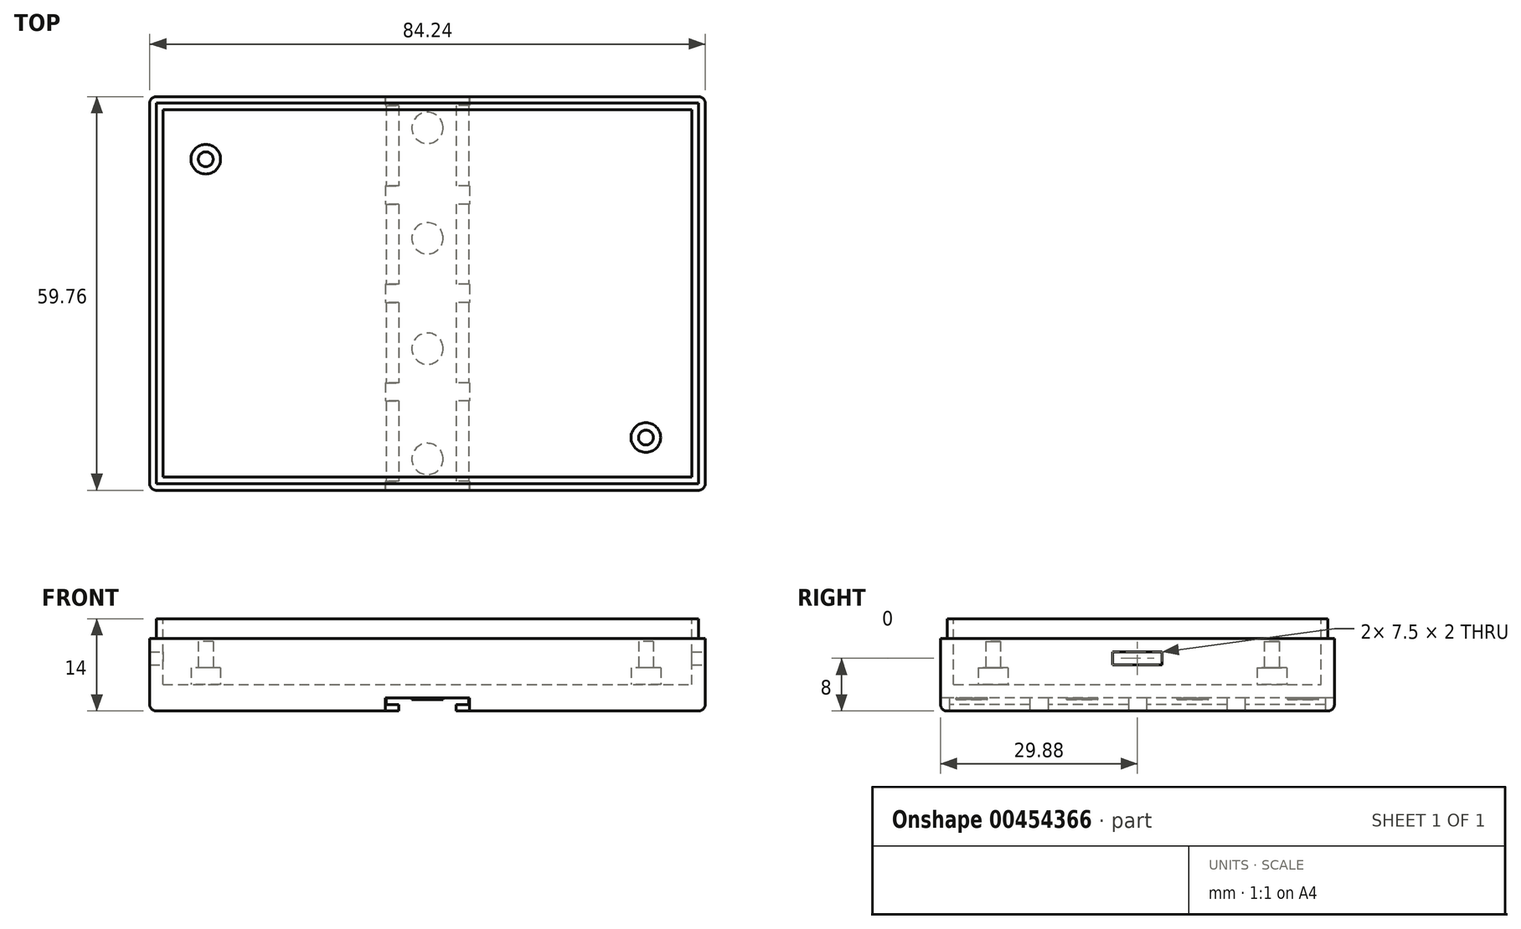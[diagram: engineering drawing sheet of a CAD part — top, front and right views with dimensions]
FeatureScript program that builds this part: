
annotation { "Feature Type Name" : "Feature", "Feature Type Description" : "" }
export const myFeature = defineFeature(function(context is Context, id is Id, definition is map)
    precondition{}
    {
        {
            var Q0;
            Q0=qCreatedBy(makeId("Top.planeOp"),FACE);
            var sketch = newSketch(context, id + "F0", { "sketchPlane" : qUnion([Q0])});
            skLineSegment(sketch, "E0.bottom", {"start": v(38.12, 25.88) * mm, "end": v(-38.12, 25.88) * mm});
            skLineSegment(sketch, "E0.top", {"start": v(38.12, -25.88) * mm, "end": v(-38.12, -25.88) * mm});
            skLineSegment(sketch, "E0.left", {"start": v(38.12, 25.88) * mm, "end": v(38.12, -25.88) * mm});
            skLineSegment(sketch, "E0.right", {"start": v(-38.12, 25.88) * mm, "end": v(-38.12, -25.88) * mm});
            skPoint(sketch, "E0.middle", {"position": v(0, 0) * mm});
            skLineSegment(sketch, "E1.bottom", {"start": v(42.13, 29.88) * mm, "end": v(-42.12, 29.87) * mm});
            skLineSegment(sketch, "E1.top", {"start": v(42.13, -29.87) * mm, "end": v(-42.12, -29.88) * mm});
            skLineSegment(sketch, "E1.left", {"start": v(42.13, 29.88) * mm, "end": v(42.13, -29.87) * mm});
            skLineSegment(sketch, "E1.right", {"start": v(-42.12, 29.87) * mm, "end": v(-42.12, -29.88) * mm});
            skSolve(sketch);
        }
        {
            var Q0;
            Q0=makeQuery(id+"F0.imprint","IMPRINT",FACE,{"disambiguationData":[TD([[makeQuery(id+"F0.imprint","IMPRINT",EDGE,{"derivedFrom":sQuery(id+"F0.wireOp",EDGE,"E0.bottom")}),1.0]])]});
            var Q1;
            Q1=makeQuery(id+"F0.imprint","IMPRINT",FACE,{"disambiguationData":[TD([[makeQuery(id+"F0.imprint","IMPRINT",EDGE,{"derivedFrom":sQuery(id+"F0.wireOp",EDGE,"E0.bottom")}),-1.0]])]});
            extrude(context, id + "F1", {"entities" : qUnion([Q0, Q1]), "depth" : 14 * mm});
        }
        {
            var Q0;
            Q0=makeQuery(id+"F1.opExtrude","CAP_FACE",FACE,{"disambiguationData":[OSD([sQuery(id+"F0.wireOp",EDGE,"E1.bottom"),sQuery(id+"F0.wireOp",EDGE,"E1.top"),sQuery(id+"F0.wireOp",EDGE,"E1.left"),sQuery(id+"F0.wireOp",EDGE,"E1.right")])],"isStart":false});
            var sketch = newSketch(context, id + "F2", { "sketchPlane" : qUnion([Q0])});
            skLineSegment(sketch, "E2.0", {"start": v(-40.12, -27.88) * mm, "end": v(40.13, -27.87) * mm});
            skLineSegment(sketch, "E2.1", {"start": v(-40.12, 27.87) * mm, "end": v(-40.12, -27.88) * mm});
            skLineSegment(sketch, "E2.2", {"start": v(40.13, 27.88) * mm, "end": v(-40.12, 27.87) * mm});
            skLineSegment(sketch, "E2.3", {"start": v(40.13, -27.87) * mm, "end": v(40.13, 27.88) * mm});
            skSolve(sketch);
        }
        {
            var Q0;
            Q0=makeQuery(id+"F2.imprint","IMPRINT",FACE,{"disambiguationData":[TD([[makeQuery(id+"F2.imprint","IMPRINT",EDGE,{"derivedFrom":sQuery(id+"F2.wireOp",EDGE,"E2.0")}),1.0]])]});
            extrude(context, id + "F3", {"entities" : qUnion([Q0]), "operationType" : NewBodyOperationType.REMOVE, "oppositeDirection" : true, "depth" : 10 * mm});
        }
        {
            var Q0;
            Q0=makeQuery(id+"F1.opExtrude","SWEPT_FACE",FACE,{"disambiguationData":[OSD([sQuery(id+"F0.wireOp",EDGE,"E1.top")])]});
            var sketch = newSketch(context, id + "F4", { "sketchPlane" : qUnion([Q0])});
            skLineSegment(sketch, "E3", {"start": v(0, 0) * mm, "end": v(-4.38, 0) * mm});
            skLineSegment(sketch, "E4", {"start": v(-4.38, 0) * mm, "end": v(-4.38, 1) * mm});
            skLineSegment(sketch, "E5", {"start": v(-4.38, 1) * mm, "end": v(-6.25, 1) * mm});
            skLineSegment(sketch, "E6", {"start": v(-6.25, 1) * mm, "end": v(-6.25, 2) * mm});
            skLineSegment(sketch, "E7", {"start": v(-6.25, 2) * mm, "end": v(0, 2) * mm});
            skLineSegment(sketch, "E8", {"start": v(0, 2) * mm, "end": v(0, 0) * mm});
            skLineSegment(sketch, "E9.MirrorCS", {"start": v(6.25, 2) * mm, "end": v(0, 2) * mm});
            skLineSegment(sketch, "E10.MirrorCS", {"start": v(6.25, 1) * mm, "end": v(6.25, 2) * mm});
            skLineSegment(sketch, "E11.MirrorCS", {"start": v(4.38, 1) * mm, "end": v(6.25, 1) * mm});
            skLineSegment(sketch, "E12.MirrorCS", {"start": v(4.38, 0) * mm, "end": v(4.38, 1) * mm});
            skLineSegment(sketch, "E13.MirrorCS", {"start": v(0, 0) * mm, "end": v(4.38, 0) * mm});
            skSolve(sketch);
        }
        {
            var Q0;
            Q0=makeQuery(id+"F4.imprint","IMPRINT",FACE,{"disambiguationData":[TD([[makeQuery(id+"F4.imprint","IMPRINT",EDGE,{"derivedFrom":sQuery(id+"F4.wireOp",EDGE,"E3")}),-1.0]])]});
            var Q1;
            Q1=makeQuery(id+"F4.imprint","IMPRINT",FACE,{"disambiguationData":[TD([[makeQuery(id+"F4.imprint","IMPRINT",EDGE,{"derivedFrom":sQuery(id+"F4.wireOp",EDGE,"E8")}),1.0]])]});
            extrude(context, id + "F5", {"entities" : qUnion([Q0, Q1]), "operationType" : NewBodyOperationType.REMOVE, "oppositeDirection" : true, "depth" : 62 * mm});
        }
        {
            var Q0;
            Q0=qCreatedBy(makeId("Top.planeOp"),FACE);
            var sketch = newSketch(context, id + "F6", { "sketchPlane" : qUnion([Q0])});
            skLineSegment(sketch, "E14.bottom", {"start": v(6.38, 1.38) * mm, "end": v(-6.38, 1.38) * mm});
            skLineSegment(sketch, "E14.top", {"start": v(6.38, -1.38) * mm, "end": v(-6.38, -1.38) * mm});
            skLineSegment(sketch, "E14.left", {"start": v(6.38, 1.38) * mm, "end": v(6.38, -1.38) * mm});
            skLineSegment(sketch, "E14.right", {"start": v(-6.38, 1.38) * mm, "end": v(-6.38, -1.38) * mm});
            skPoint(sketch, "E14.middle", {"position": v(0, 0) * mm});
            skLineSegment(sketch, "E15.0.1.0", {"start": v(6.38, 16.31) * mm, "end": v(-6.38, 16.31) * mm});
            skLineSegment(sketch, "E15.0.1.1", {"start": v(-6.38, 16.31) * mm, "end": v(-6.38, 13.56) * mm});
            skLineSegment(sketch, "E15.0.1.2", {"start": v(6.38, 16.31) * mm, "end": v(6.38, 13.56) * mm});
            skLineSegment(sketch, "E15.0.1.3", {"start": v(6.38, 13.56) * mm, "end": v(-6.38, 13.56) * mm});
            skLineSegment(sketch, "E15.0.2.0", {"start": v(6.38, 31.25) * mm, "end": v(-6.38, 31.25) * mm});
            skLineSegment(sketch, "E15.0.2.1", {"start": v(-6.38, 31.25) * mm, "end": v(-6.38, 28.5) * mm});
            skLineSegment(sketch, "E15.0.2.2", {"start": v(6.38, 31.25) * mm, "end": v(6.38, 28.5) * mm});
            skLineSegment(sketch, "E15.0.2.3", {"start": v(6.38, 28.5) * mm, "end": v(-6.38, 28.5) * mm});
            skLineSegment(sketch, "E15.direction1", {"start": v(-6.38, -1.38) * mm, "end": v(18.63, -1.38) * mm, "construction": true});
            skLineSegment(sketch, "E15.direction2", {"start": v(-6.38, -1.38) * mm, "end": v(-6.38, 13.56) * mm, "construction": true});
            skLineSegment(sketch, "E16.0.1.0", {"start": v(6.38, -13.56) * mm, "end": v(-6.38, -13.56) * mm});
            skLineSegment(sketch, "E16.0.1.1", {"start": v(6.38, -13.56) * mm, "end": v(6.38, -16.31) * mm});
            skPoint(sketch, "E16.0.1.2", {"position": v(0, -14.94) * mm});
            skLineSegment(sketch, "E16.0.1.3", {"start": v(6.38, -16.31) * mm, "end": v(-6.38, -16.31) * mm});
            skLineSegment(sketch, "E16.0.1.4", {"start": v(-6.38, -13.56) * mm, "end": v(-6.38, -16.31) * mm});
            skLineSegment(sketch, "E16.0.2.0", {"start": v(6.38, -28.5) * mm, "end": v(-6.38, -28.5) * mm});
            skLineSegment(sketch, "E16.0.2.1", {"start": v(6.38, -28.5) * mm, "end": v(6.38, -31.25) * mm});
            skPoint(sketch, "E16.0.2.2", {"position": v(0, -29.88) * mm});
            skLineSegment(sketch, "E16.0.2.3", {"start": v(6.38, -31.25) * mm, "end": v(-6.38, -31.25) * mm});
            skLineSegment(sketch, "E16.0.2.4", {"start": v(-6.38, -28.5) * mm, "end": v(-6.38, -31.25) * mm});
            skLineSegment(sketch, "E16.direction2", {"start": v(-6.38, -1.38) * mm, "end": v(-6.38, -16.31) * mm, "construction": true});
            skSolve(sketch);
        }
        {
            var Q0;
            Q0=makeQuery(id+"F6.imprint","IMPRINT",FACE,{"disambiguationData":[TD([[makeQuery(id+"F6.imprint","IMPRINT",EDGE,{"derivedFrom":sQuery(id+"F6.wireOp",EDGE,"E15.0.2.0")}),1.0]])]});
            var Q1;
            Q1=makeQuery(id+"F6.imprint","IMPRINT",FACE,{"disambiguationData":[TD([[makeQuery(id+"F6.imprint","IMPRINT",EDGE,{"derivedFrom":sQuery(id+"F6.wireOp",EDGE,"E15.0.1.0")}),1.0]])]});
            var Q2;
            Q2=makeQuery(id+"F6.imprint","IMPRINT",FACE,{"disambiguationData":[TD([[makeQuery(id+"F6.imprint","IMPRINT",EDGE,{"derivedFrom":sQuery(id+"F6.wireOp",EDGE,"E14.bottom")}),1.0]])]});
            var Q3;
            Q3=makeQuery(id+"F6.imprint","IMPRINT",FACE,{"disambiguationData":[TD([[makeQuery(id+"F6.imprint","IMPRINT",EDGE,{"derivedFrom":sQuery(id+"F6.wireOp",EDGE,"E16.0.1.0")}),1.0]])]});
            var Q4;
            Q4=makeQuery(id+"F6.imprint","IMPRINT",FACE,{"disambiguationData":[TD([[makeQuery(id+"F6.imprint","IMPRINT",EDGE,{"derivedFrom":sQuery(id+"F6.wireOp",EDGE,"E16.0.2.0")}),1.0]])]});
            extrude(context, id + "F7", {"entities" : qUnion([Q0, Q1, Q2, Q3, Q4]), "operationType" : NewBodyOperationType.REMOVE, "oppositeDirection" : true, "depth" : -2 * mm});
        }
        {
            var Q0;
            Q0=makeQuery(id+"F7.boolean.opBoolean","MERGE",FACE,{"derivedFrom":[makeQuery(id+"F5.boolean.opBoolean","COPY",FACE,{"derivedFrom":makeQuery(id+"F5.opExtrude","SWEPT_FACE",FACE,{"disambiguationData":[OSD([sQuery(id+"F4.wireOp",EDGE,"E7"),sQuery(id+"F4.wireOp",EDGE,"E9.MirrorCS")])]})}),makeQuery(id+"F7.opExtrude","CAP_FACE",FACE,{"disambiguationData":[OSD([sQuery(id+"F6.wireOp",EDGE,"E14.bottom"),sQuery(id+"F6.wireOp",EDGE,"E14.top"),sQuery(id+"F6.wireOp",EDGE,"E14.left"),sQuery(id+"F6.wireOp",EDGE,"E14.right")])],"isStart":false}),makeQuery(id+"F7.opExtrude","CAP_FACE",FACE,{"disambiguationData":[OSD([sQuery(id+"F6.wireOp",EDGE,"E15.0.1.0"),sQuery(id+"F6.wireOp",EDGE,"E15.0.1.1"),sQuery(id+"F6.wireOp",EDGE,"E15.0.1.2"),sQuery(id+"F6.wireOp",EDGE,"E15.0.1.3")])],"isStart":false}),makeQuery(id+"F7.opExtrude","CAP_FACE",FACE,{"disambiguationData":[OSD([sQuery(id+"F6.wireOp",EDGE,"E15.0.2.0"),sQuery(id+"F6.wireOp",EDGE,"E15.0.2.1"),sQuery(id+"F6.wireOp",EDGE,"E15.0.2.2"),sQuery(id+"F6.wireOp",EDGE,"E15.0.2.3")])],"isStart":false}),makeQuery(id+"F7.opExtrude","CAP_FACE",FACE,{"disambiguationData":[OSD([sQuery(id+"F6.wireOp",EDGE,"E16.0.1.0"),sQuery(id+"F6.wireOp",EDGE,"E16.0.1.1"),sQuery(id+"F6.wireOp",EDGE,"E16.0.1.3"),sQuery(id+"F6.wireOp",EDGE,"E16.0.1.4")])],"isStart":false}),makeQuery(id+"F7.opExtrude","CAP_FACE",FACE,{"disambiguationData":[OSD([sQuery(id+"F6.wireOp",EDGE,"E16.0.2.0"),sQuery(id+"F6.wireOp",EDGE,"E16.0.2.1"),sQuery(id+"F6.wireOp",EDGE,"E16.0.2.3"),sQuery(id+"F6.wireOp",EDGE,"E16.0.2.4")])],"isStart":false})]});
            var sketch = newSketch(context, id + "F8", { "sketchPlane" : qUnion([Q0])});
            skCircle(sketch, "E17", {"center": v(0, 25.12) * mm, "radius": 2.38 * mm});
            skCircle(sketch, "E18.0.1.0", {"center": v(0, 8.37) * mm, "radius": 2.38 * mm});
            skCircle(sketch, "E18.0.2.0", {"center": v(0, -8.38) * mm, "radius": 2.38 * mm});
            skCircle(sketch, "E18.0.3.0", {"center": v(0, -25.13) * mm, "radius": 2.38 * mm});
            skLineSegment(sketch, "E18.direction1", {"start": v(0, 25.12) * mm, "end": v(25, 25.12) * mm, "construction": true});
            skLineSegment(sketch, "E18.direction2", {"start": v(0, 25.12) * mm, "end": v(0, 8.37) * mm, "construction": true});
            skSolve(sketch);
        }
        {
            var Q0;
            Q0=makeQuery(id+"F8.imprint","IMPRINT",FACE,{"disambiguationData":[TD([[makeQuery(id+"F8.imprint","IMPRINT",EDGE,{"derivedFrom":sQuery(id+"F8.wireOp",EDGE,"E17")}),1.0]])]});
            var Q1;
            Q1=makeQuery(id+"F8.imprint","IMPRINT",FACE,{"disambiguationData":[TD([[makeQuery(id+"F8.imprint","IMPRINT",EDGE,{"derivedFrom":sQuery(id+"F8.wireOp",EDGE,"E18.0.1.0")}),1.0]])]});
            var Q2;
            Q2=makeQuery(id+"F8.imprint","IMPRINT",FACE,{"disambiguationData":[TD([[makeQuery(id+"F8.imprint","IMPRINT",EDGE,{"derivedFrom":sQuery(id+"F8.wireOp",EDGE,"E18.0.2.0")}),1.0]])]});
            var Q3;
            Q3=makeQuery(id+"F8.imprint","IMPRINT",FACE,{"disambiguationData":[TD([[makeQuery(id+"F8.imprint","IMPRINT",EDGE,{"derivedFrom":sQuery(id+"F8.wireOp",EDGE,"E18.0.3.0")}),1.0]])]});
            var Q4;
            Q4=sQuery(id+"F8.wireOp",EDGE,"E18.0.1.0");
            var Q5;
            Q5=sQuery(id+"F8.wireOp",EDGE,"E17");
            var Q6;
            Q6=sQuery(id+"F8.wireOp",EDGE,"E18.0.2.0");
            var Q7;
            Q7=sQuery(id+"F8.wireOp",EDGE,"E18.0.3.0");
            extrude(context, id + "F9", {"entities" : qUnion([Q0, Q1, Q2, Q3]), "operationType" : NewBodyOperationType.ADD, "surfaceEntities" : qUnion([Q4, Q5, Q6, Q7]), "depth" : 0.25 * mm});
        }
        {
            var Q0;
            Q0=makeQuery(id+"F1.opExtrude","CAP_FACE",FACE,{"disambiguationData":[OSD([sQuery(id+"F0.wireOp",EDGE,"E1.bottom"),sQuery(id+"F0.wireOp",EDGE,"E1.top"),sQuery(id+"F0.wireOp",EDGE,"E1.left"),sQuery(id+"F0.wireOp",EDGE,"E1.right")])],"isStart":false});
            var sketch = newSketch(context, id + "F10", { "sketchPlane" : qUnion([Q0])});
            skLineSegment(sketch, "E19.0", {"start": v(-41.12, -28.88) * mm, "end": v(41.13, -28.87) * mm});
            skLineSegment(sketch, "E19.1", {"start": v(-41.12, 28.87) * mm, "end": v(-41.12, -28.88) * mm});
            skLineSegment(sketch, "E19.2", {"start": v(41.13, 28.88) * mm, "end": v(-41.12, 28.87) * mm});
            skLineSegment(sketch, "E19.3", {"start": v(41.13, -28.87) * mm, "end": v(41.13, 28.88) * mm});
            skSolve(sketch);
        }
        {
            var Q0;
            Q0=makeQuery(id+"F10.imprint","IMPRINT",FACE,{"disambiguationData":[TD([[makeQuery(id+"F10.imprint","IMPRINT",EDGE,{"derivedFrom":sQuery(id+"F10.wireOp",EDGE,"E19.0")}),-1.0]])]});
            extrude(context, id + "F11", {"entities" : qUnion([Q0]), "operationType" : NewBodyOperationType.REMOVE, "oppositeDirection" : true, "depth" : 3 * mm});
        }
        {
            var Q0;
            Q0=makeQuery(id+"F1.opExtrude","SWEPT_FACE",FACE,{"disambiguationData":[OSD([sQuery(id+"F0.wireOp",EDGE,"E1.left")])]});
            var sketch = newSketch(context, id + "F12", { "sketchPlane" : qUnion([Q0])});
            skLineSegment(sketch, "E20.bottom", {"start": v(3.75, 7) * mm, "end": v(-3.75, 7) * mm});
            skLineSegment(sketch, "E20.top", {"start": v(3.75, 9) * mm, "end": v(-3.75, 9) * mm});
            skLineSegment(sketch, "E20.left", {"start": v(3.75, 7) * mm, "end": v(3.75, 9) * mm});
            skLineSegment(sketch, "E20.right", {"start": v(-3.75, 7) * mm, "end": v(-3.75, 9) * mm});
            skPoint(sketch, "E20.middle", {"position": v(0, 8) * mm});
            skSolve(sketch);
        }
        {
            var Q0;
            Q0=makeQuery(id+"F12.imprint","IMPRINT",FACE,{"disambiguationData":[TD([[makeQuery(id+"F12.imprint","IMPRINT",EDGE,{"derivedFrom":sQuery(id+"F12.wireOp",EDGE,"E20.bottom")}),-1.0]])]});
            extrude(context, id + "F13", {"entities" : qUnion([Q0]), "operationType" : NewBodyOperationType.REMOVE, "oppositeDirection" : true, "depth" : 85 * mm});
        }
        {
            var Q0;
            {var subQ0=sQuery(id+"F0.wireOp",EDGE,"E1.left");var subQ1=sQuery(id+"F0.wireOp",EDGE,"E1.top");Q0=makeQuery(id+"F5.boolean.opBoolean","SPLIT",EDGE,{"disambiguationData":[TD([makeQuery(id+"F1.opExtrude","SWEPT_FACE",FACE,{"disambiguationData":[OSD([subQ0])]})])],"derivedFrom":makeQuery(id+"F1.opExtrude","CAP_EDGE",EDGE,{"disambiguationData":[OSD([subQ1])],"isStart":true})});}
            var Q1;
            Q1=makeQuery(id+"F1.opExtrude","CAP_EDGE",EDGE,{"disambiguationData":[OSD([sQuery(id+"F0.wireOp",EDGE,"E1.left")])],"isStart":true});
            var Q2;
            {var subQ0=sQuery(id+"F0.wireOp",EDGE,"E1.bottom");var subQ1=sQuery(id+"F0.wireOp",EDGE,"E1.left");Q2=makeQuery(id+"F5.boolean.opBoolean","SPLIT",EDGE,{"disambiguationData":[TD([makeQuery(id+"F1.opExtrude","SWEPT_FACE",FACE,{"disambiguationData":[OSD([subQ1])]})])],"derivedFrom":makeQuery(id+"F1.opExtrude","CAP_EDGE",EDGE,{"disambiguationData":[OSD([subQ0])],"isStart":true})});}
            var Q3;
            {var subQ0=sQuery(id+"F0.wireOp",EDGE,"E1.bottom");var subQ1=sQuery(id+"F0.wireOp",EDGE,"E1.right");Q3=makeQuery(id+"F5.boolean.opBoolean","SPLIT",EDGE,{"disambiguationData":[TD([makeQuery(id+"F1.opExtrude","SWEPT_FACE",FACE,{"disambiguationData":[OSD([subQ1])]})])],"derivedFrom":makeQuery(id+"F1.opExtrude","CAP_EDGE",EDGE,{"disambiguationData":[OSD([subQ0])],"isStart":true})});}
            var Q4;
            Q4=makeQuery(id+"F1.opExtrude","CAP_EDGE",EDGE,{"disambiguationData":[OSD([sQuery(id+"F0.wireOp",EDGE,"E1.right")])],"isStart":true});
            var Q5;
            {var subQ0=sQuery(id+"F0.wireOp",EDGE,"E1.right");var subQ1=sQuery(id+"F0.wireOp",EDGE,"E1.top");Q5=makeQuery(id+"F5.boolean.opBoolean","SPLIT",EDGE,{"disambiguationData":[TD([makeQuery(id+"F1.opExtrude","SWEPT_FACE",FACE,{"disambiguationData":[OSD([subQ0])]})])],"derivedFrom":makeQuery(id+"F1.opExtrude","CAP_EDGE",EDGE,{"disambiguationData":[OSD([subQ1])],"isStart":true})});}
            var Q6;
            Q6=makeQuery(id+"F1.opExtrude","SWEPT_EDGE",EDGE,{"disambiguationData":[OSD([sQuery(id+"F0.wireOp",EDGE,"E1.top"),sQuery(id+"F0.wireOp",EDGE,"E1.left")])]});
            var Q7;
            Q7=makeQuery(id+"F1.opExtrude","SWEPT_EDGE",EDGE,{"disambiguationData":[OSD([sQuery(id+"F0.wireOp",EDGE,"E1.bottom"),sQuery(id+"F0.wireOp",EDGE,"E1.left")])]});
            var Q8;
            Q8=makeQuery(id+"F1.opExtrude","SWEPT_EDGE",EDGE,{"disambiguationData":[OSD([sQuery(id+"F0.wireOp",EDGE,"E1.top"),sQuery(id+"F0.wireOp",EDGE,"E1.right")])]});
            var Q9;
            Q9=makeQuery(id+"F1.opExtrude","SWEPT_EDGE",EDGE,{"disambiguationData":[OSD([sQuery(id+"F0.wireOp",EDGE,"E1.bottom"),sQuery(id+"F0.wireOp",EDGE,"E1.right")])]});
            fillet(context, id + "F14", {"entities" : qUnion([Q0, Q1, Q2, Q3, Q4, Q5, Q6, Q7, Q8, Q9]), "radius" : 1 * mm, "tangentPropagation" : true, "allowEdgeOverflow" : false});
        }
        {
            var Q0;
            Q0=makeQuery(id+"F3.boolean.opBoolean","COPY",FACE,{"derivedFrom":makeQuery(id+"F3.opExtrude","CAP_FACE",FACE,{"disambiguationData":[OSD([sQuery(id+"F2.wireOp",EDGE,"E2.0"),sQuery(id+"F2.wireOp",EDGE,"E2.1"),sQuery(id+"F2.wireOp",EDGE,"E2.2"),sQuery(id+"F2.wireOp",EDGE,"E2.3")])],"isStart":false})});
            var sketch = newSketch(context, id + "F15", { "sketchPlane" : qUnion([Q0])});
            skLineSegment(sketch, "E21.bottom", {"start": v(38.12, 25.88) * mm, "end": v(-38.12, 25.88) * mm});
            skLineSegment(sketch, "E21.top", {"start": v(38.12, -25.88) * mm, "end": v(-38.12, -25.88) * mm});
            skLineSegment(sketch, "E21.left", {"start": v(38.12, 25.88) * mm, "end": v(38.12, -25.88) * mm});
            skLineSegment(sketch, "E21.right", {"start": v(-38.12, 25.88) * mm, "end": v(-38.12, -25.88) * mm});
            skPoint(sketch, "E21.middle", {"position": v(0, 0) * mm});
            skCircle(sketch, "E22", {"center": v(-33.62, 20.38) * mm, "radius": 2.25 * mm});
            skCircle(sketch, "E23", {"center": v(33.12, -21.88) * mm, "radius": 2.25 * mm});
            skSolve(sketch);
        }
        {
            var Q0;
            Q0=makeQuery(id+"F15.imprint","IMPRINT",FACE,{"disambiguationData":[TD([[makeQuery(id+"F15.imprint","IMPRINT",EDGE,{"derivedFrom":sQuery(id+"F15.wireOp",EDGE,"E22")}),1.0]])]});
            extrude(context, id + "F16", {"entities" : qUnion([Q0]), "operationType" : NewBodyOperationType.ADD, "depth" : 2.54 * mm});
        }
        {
            var Q0;
            Q0=makeQuery(id+"F16.opExtrude","CAP_FACE",FACE,{"disambiguationData":[OSD([sQuery(id+"F15.wireOp",EDGE,"E22")])],"isStart":false});
            var sketch = newSketch(context, id + "F17", { "sketchPlane" : qUnion([Q0])});
            skCircle(sketch, "E24.0", {"center": v(-33.62, 20.38) * mm, "radius": 1.13 * mm});
            skSolve(sketch);
        }
        {
            var Q0;
            Q0=makeQuery(id+"F17.imprint","IMPRINT",FACE,{"disambiguationData":[TD([[makeQuery(id+"F17.imprint","IMPRINT",EDGE,{"derivedFrom":sQuery(id+"F17.wireOp",EDGE,"E24.0")}),1.0]])]});
            extrude(context, id + "F18", {"entities" : qUnion([Q0]), "operationType" : NewBodyOperationType.ADD, "depth" : 4 * mm});
        }
        {
            var Q0;
            Q0=makeQuery(id+"F15.imprint","IMPRINT",FACE,{"disambiguationData":[TD([[makeQuery(id+"F15.imprint","IMPRINT",EDGE,{"derivedFrom":sQuery(id+"F15.wireOp",EDGE,"E23")}),1.0]])]});
            extrude(context, id + "F19", {"entities" : qUnion([Q0]), "operationType" : NewBodyOperationType.ADD, "depth" : 2.54 * mm});
        }
        {
            var Q0;
            Q0=makeQuery(id+"F19.opExtrude","CAP_FACE",FACE,{"disambiguationData":[OSD([sQuery(id+"F15.wireOp",EDGE,"E23")])],"isStart":false});
            var sketch = newSketch(context, id + "F20", { "sketchPlane" : qUnion([Q0])});
            skCircle(sketch, "E25.0", {"center": v(33.12, -21.88) * mm, "radius": 1.13 * mm});
            skSolve(sketch);
        }
        {
            var Q0;
            Q0=makeQuery(id+"F20.imprint","IMPRINT",FACE,{"disambiguationData":[TD([[makeQuery(id+"F20.imprint","IMPRINT",EDGE,{"derivedFrom":sQuery(id+"F20.wireOp",EDGE,"E25.0")}),1.0]])]});
            extrude(context, id + "F21", {"entities" : qUnion([Q0]), "operationType" : NewBodyOperationType.ADD, "depth" : 4 * mm});
        }
    });
